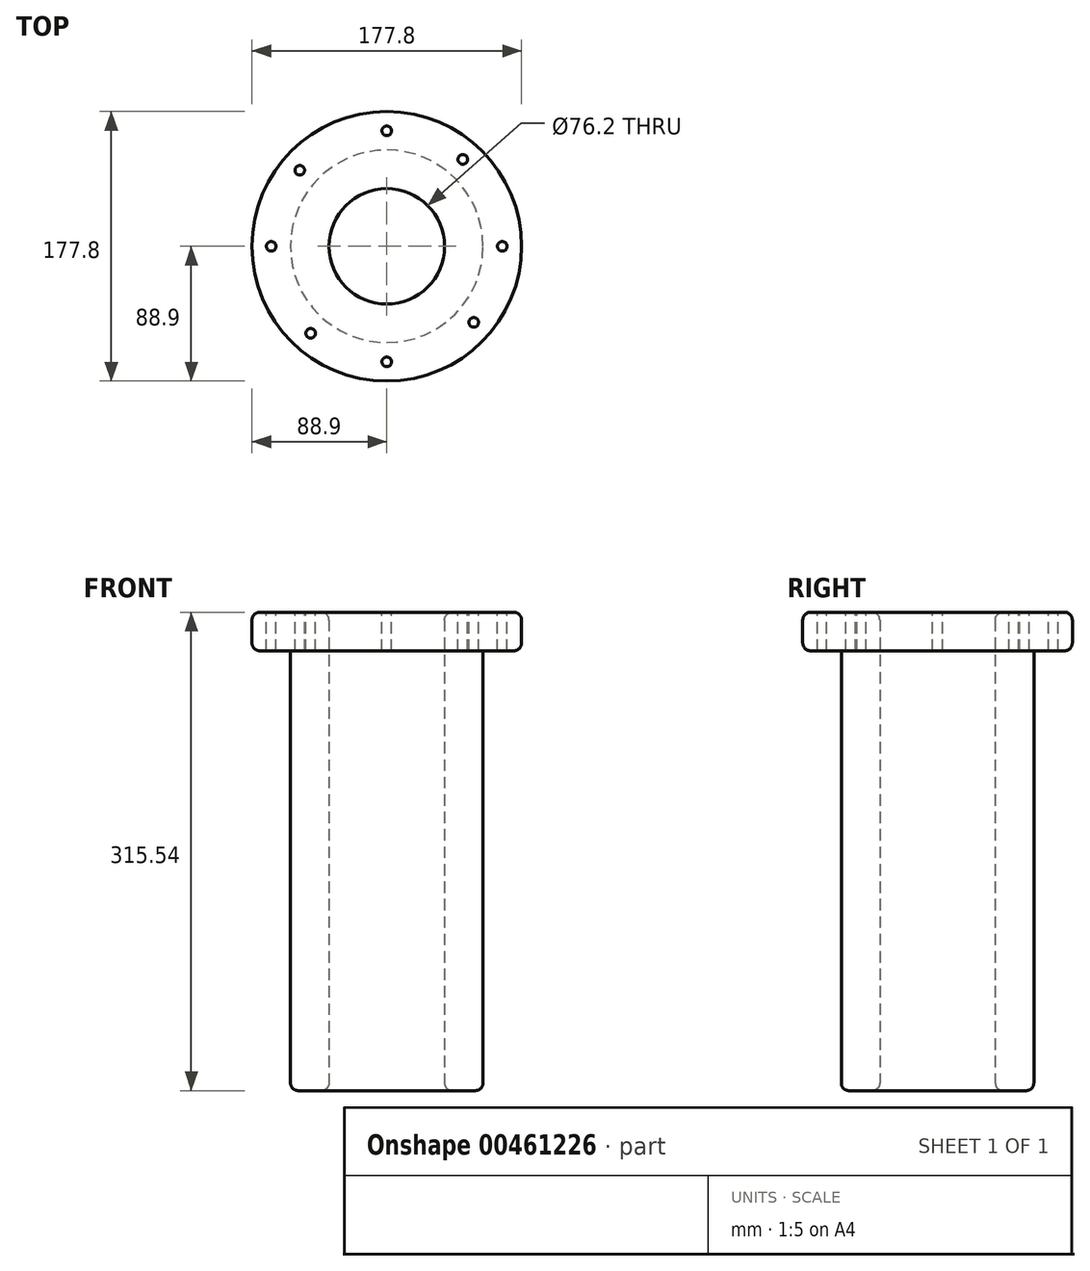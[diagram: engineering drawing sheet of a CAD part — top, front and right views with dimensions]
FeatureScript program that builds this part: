
annotation { "Feature Type Name" : "Feature", "Feature Type Description" : "" }
export const myFeature = defineFeature(function(context is Context, id is Id, definition is map)
    precondition{}
    {
        {
            var Q0;
            Q0=qCreatedBy(makeId("Front.planeOp"),FACE);
            var sketch = newSketch(context, id + "F0", { "sketchPlane" : qUnion([Q0])});
            skLineSegment(sketch, "E0.bottom", {"start": v(63.5, -145.07) * mm, "end": v(-63.5, -145.07) * mm});
            skLineSegment(sketch, "E0.top", {"start": v(63.5, 145.07) * mm, "end": v(-63.5, 145.07) * mm});
            skLineSegment(sketch, "E0.left", {"start": v(63.5, -145.07) * mm, "end": v(63.5, 145.07) * mm});
            skLineSegment(sketch, "E0.right", {"start": v(-63.5, -145.07) * mm, "end": v(-63.5, 145.07) * mm});
            skPoint(sketch, "E0.middle", {"position": v(0, 0) * mm});
            skLineSegment(sketch, "E1", {"start": v(0, 145.07) * mm, "end": v(0, -145.07) * mm});
            skLineSegment(sketch, "E2", {"start": v(-38.1, -145.07) * mm, "end": v(-38.1, 145.07) * mm});
            skLineSegment(sketch, "E3", {"start": v(38.1, 145.07) * mm, "end": v(38.1, -145.07) * mm});
            skLineSegment(sketch, "E4", {"start": v(-88.9, 145.07) * mm, "end": v(38.1, 145.07) * mm});
            skLineSegment(sketch, "E5", {"start": v(38.1, 145.07) * mm, "end": v(38.1, 170.47) * mm});
            skLineSegment(sketch, "E6", {"start": v(38.1, 170.47) * mm, "end": v(-88.9, 170.47) * mm});
            skLineSegment(sketch, "E7", {"start": v(-88.9, 170.47) * mm, "end": v(-88.9, 145.07) * mm});
            skLineSegment(sketch, "E8", {"start": v(-38.1, 145.07) * mm, "end": v(-38.1, 170.47) * mm});
            skLineSegment(sketch, "E9", {"start": v(0, 145.07) * mm, "end": v(0, 170.47) * mm});
            skLineSegment(sketch, "E10", {"start": v(0, 170.47) * mm, "end": v(88.9, 170.47) * mm});
            skLineSegment(sketch, "E11", {"start": v(88.9, 170.47) * mm, "end": v(88.9, 145.07) * mm});
            skLineSegment(sketch, "E12", {"start": v(88.9, 145.07) * mm, "end": v(63.5, 145.07) * mm});
            skSolve(sketch);
        }
        {
            var Q0;
            {var subQ0=sQuery(id+"F0.wireOp",EDGE,"E7");Q0=makeQuery(id+"F0.imprint","IMPRINT",FACE,{"disambiguationData":[TD([[makeQuery(id+"F0.imprint","IMPRINT",EDGE,{"derivedFrom":subQ0}),1.0]])]});}
            var Q1;
            Q1=sQuery(id+"F0.wireOp",EDGE,"E9");
            revolve(context, id + "F1", {"entities" : qUnion([Q0]), "axis" : qUnion([Q1]), "revolveType" : RevolveType.FULL});
        }
        {
            var Q0;
            {var subQ0=sQuery(id+"F0.wireOp",EDGE,"E0.right");Q0=makeQuery(id+"F0.imprint","IMPRINT",FACE,{"disambiguationData":[TD([[makeQuery(id+"F0.imprint","IMPRINT",EDGE,{"derivedFrom":subQ0}),-1.0]])]});}
            var Q1;
            Q1=sQuery(id+"F0.wireOp",EDGE,"E1");
            revolve(context, id + "F2", {"operationType" : NewBodyOperationType.ADD, "entities" : qUnion([Q0]), "axis" : qUnion([Q1]), "revolveType" : RevolveType.FULL});
        }
        {
            var Q0;
            Q0=makeQuery(id+"F1.opRevolve","SWEPT_EDGE",EDGE,{"disambiguationData":[OSD([sQuery(id+"F0.wireOp",EDGE,"E6"),sQuery(id+"F0.wireOp",EDGE,"E7")])]});
            var Q1;
            Q1=makeQuery(id+"F1.opRevolve","SWEPT_EDGE",EDGE,{"disambiguationData":[OSD([sQuery(id+"F0.wireOp",EDGE,"E4"),sQuery(id+"F0.wireOp",EDGE,"E7")])]});
            var Q2;
            Q2=makeQuery(id+"F1.opRevolve","SWEPT_EDGE",EDGE,{"disambiguationData":[OSD([sQuery(id+"F0.wireOp",EDGE,"E6"),sQuery(id+"F0.wireOp",EDGE,"E8")])]});
            var Q3;
            Q3=makeQuery(id+"F2.opRevolve","SWEPT_EDGE",EDGE,{"disambiguationData":[OSD([sQuery(id+"F0.wireOp",EDGE,"E0.bottom"),sQuery(id+"F0.wireOp",EDGE,"E0.right")])]});
            fillet(context, id + "F3", {"entities" : qUnion([Q0, Q1, Q2, Q3]), "radius" : 5.08 * mm, "tangentPropagation" : true, "allowEdgeOverflow" : false});
        }
        {
            var Q0;
            Q0=makeQuery(id+"F2.opRevolve","SWEPT_EDGE",EDGE,{"disambiguationData":[OSD([sQuery(id+"F0.wireOp",EDGE,"E0.bottom"),sQuery(id+"F0.wireOp",EDGE,"E2")])]});
            fillet(context, id + "F4", {"entities" : qUnion([Q0]), "radius" : 5.08 * mm, "tangentPropagation" : true, "allowEdgeOverflow" : false});
        }
        {
            var Q0;
            Q0=makeQuery(id+"F1.opRevolve","SWEPT_FACE",FACE,{"disambiguationData":[OSD([sQuery(id+"F0.wireOp",EDGE,"E6")])]});
            var sketch = newSketch(context, id + "F5", { "sketchPlane" : qUnion([Q0])});
            skLineSegment(sketch, "E13", {"start": v(0, -65.27) * mm, "end": v(0, 65.55) * mm});
            skLineSegment(sketch, "E14", {"start": v(-63.5, 0) * mm, "end": v(64.05, 0) * mm});
            skSolve(sketch);
        }
        {
            var Q0;
            {var subQ1=sQuery(id+"F0.wireOp",EDGE,"E6");var subQ2=makeQuery(id+"F1.opRevolve","SWEPT_FACE",FACE,{"disambiguationData":[OSD([subQ1])]});Q0=makeQuery(id+"F5.imprint","IMPRINT",FACE,{"disambiguationData":[TD([[makeQuery(id+"F5.imprint","IMPRINT",EDGE,{"derivedFrom":makeQuery(id+"F3.opFillet","BLEND_EDGE",EDGE,{"blendedFrom":[makeQuery(id+"F1.opRevolve","SWEPT_EDGE",EDGE,{"disambiguationData":[OSD([subQ1,sQuery(id+"F0.wireOp",EDGE,"E7")])]}),subQ2],"blendedInto":[subQ2]})}),1.0]])]});}
            var sketch = newSketch(context, id + "F6", { "sketchPlane" : qUnion([Q0])});
            skLineSegment(sketch, "E15", {"start": v(0, 0) * mm, "end": v(0, 76.2) * mm});
            skLineSegment(sketch, "E16", {"start": v(0, 0) * mm, "end": v(76.2, 0) * mm});
            skLineSegment(sketch, "E17", {"start": v(0, 0) * mm, "end": v(-76.2, 0) * mm});
            skLineSegment(sketch, "E18", {"start": v(0, 0) * mm, "end": v(0, -76.2) * mm});
            skSolve(sketch);
        }
        {
            var Q0;
            Q0=sQuery(id+"F6.wireOp",VERTEX,"E17.end");
            var Q1;
            Q1=sQuery(id+"F6.wireOp",VERTEX,"E15.end");
            var Q2;
            Q2=makeQuery(id+"F1.opRevolve","SWEPT_BODY",BODY,{"disambiguationData":[OSD([sQuery(id+"F0.wireOp",EDGE,"E4"),sQuery(id+"F0.wireOp",EDGE,"E6"),sQuery(id+"F0.wireOp",EDGE,"E7"),sQuery(id+"F0.wireOp",EDGE,"E8")])]});
            hole(context, id + "F7", {"style" : HoleStyle.SIMPLE, "endStyle" : HoleEndStyle.THROUGH, "holeDiameter" : 6.35 * mm, "isTappedThrough" : true, "tappedDepth" : 12.7 * mm, "tapClearance" : 3, "locations" : qUnion([Q0, Q1]), "scope" : qUnion([Q2])});
        }
        {
            var Q0;
            {var subQ1=sQuery(id+"F0.wireOp",EDGE,"E6");var subQ2=makeQuery(id+"F1.opRevolve","SWEPT_FACE",FACE,{"disambiguationData":[OSD([subQ1])]});Q0=makeQuery(id+"F5.imprint","IMPRINT",FACE,{"disambiguationData":[TD([[makeQuery(id+"F5.imprint","IMPRINT",EDGE,{"derivedFrom":makeQuery(id+"F3.opFillet","BLEND_EDGE",EDGE,{"blendedFrom":[makeQuery(id+"F1.opRevolve","SWEPT_EDGE",EDGE,{"disambiguationData":[OSD([subQ1,sQuery(id+"F0.wireOp",EDGE,"E7")])]}),subQ2],"blendedInto":[subQ2]})}),1.0]])]});}
            var sketch = newSketch(context, id + "F8", { "sketchPlane" : qUnion([Q0])});
            skLineSegment(sketch, "E19", {"start": v(0, 0) * mm, "end": v(0, -76.2) * mm});
            skLineSegment(sketch, "E20", {"start": v(0, 0) * mm, "end": v(76.2, 0) * mm});
            skSolve(sketch);
        }
        {
            var Q0;
            Q0=sQuery(id+"F8.wireOp",VERTEX,"E19.end");
            var Q1;
            Q1=sQuery(id+"F8.wireOp",VERTEX,"E20.end");
            var Q2;
            Q2=makeQuery(id+"F1.opRevolve","SWEPT_BODY",BODY,{"disambiguationData":[OSD([sQuery(id+"F0.wireOp",EDGE,"E4"),sQuery(id+"F0.wireOp",EDGE,"E6"),sQuery(id+"F0.wireOp",EDGE,"E7"),sQuery(id+"F0.wireOp",EDGE,"E8")])]});
            hole(context, id + "F9", {"style" : HoleStyle.SIMPLE, "endStyle" : HoleEndStyle.THROUGH, "holeDiameter" : 6.35 * mm, "isTappedThrough" : true, "tappedDepth" : 12.7 * mm, "tapClearance" : 3, "locations" : qUnion([Q0, Q1]), "scope" : qUnion([Q2])});
        }
        {
            var Q0;
            {var subQ1=sQuery(id+"F0.wireOp",EDGE,"E6");var subQ2=makeQuery(id+"F1.opRevolve","SWEPT_FACE",FACE,{"disambiguationData":[OSD([subQ1])]});Q0=makeQuery(id+"F5.imprint","IMPRINT",FACE,{"disambiguationData":[TD([[makeQuery(id+"F5.imprint","IMPRINT",EDGE,{"derivedFrom":makeQuery(id+"F3.opFillet","BLEND_EDGE",EDGE,{"blendedFrom":[makeQuery(id+"F1.opRevolve","SWEPT_EDGE",EDGE,{"disambiguationData":[OSD([subQ1,sQuery(id+"F0.wireOp",EDGE,"E7")])]}),subQ2],"blendedInto":[subQ2]})}),1.0]])]});}
            var sketch = newSketch(context, id + "F10", { "sketchPlane" : qUnion([Q0])});
            skLineSegment(sketch, "E21", {"start": v(0, 0) * mm, "end": v(-57.36, 50.16) * mm});
            skLineSegment(sketch, "E22", {"start": v(0, 0) * mm, "end": v(50.16, 57.36) * mm});
            skLineSegment(sketch, "E23", {"start": v(0, 0) * mm, "end": v(-50.16, -57.36) * mm});
            skLineSegment(sketch, "E24", {"start": v(0, 0) * mm, "end": v(57.36, -50.16) * mm});
            skSolve(sketch);
        }
        {
            var Q0;
            Q0=sQuery(id+"F10.wireOp",VERTEX,"E21.end");
            var Q1;
            Q1=sQuery(id+"F10.wireOp",VERTEX,"E22.end");
            var Q2;
            Q2=sQuery(id+"F10.wireOp",VERTEX,"E24.end");
            var Q3;
            Q3=sQuery(id+"F10.wireOp",VERTEX,"E23.end");
            var Q4;
            Q4=makeQuery(id+"F1.opRevolve","SWEPT_BODY",BODY,{"disambiguationData":[OSD([sQuery(id+"F0.wireOp",EDGE,"E4"),sQuery(id+"F0.wireOp",EDGE,"E6"),sQuery(id+"F0.wireOp",EDGE,"E7"),sQuery(id+"F0.wireOp",EDGE,"E8")])]});
            hole(context, id + "F11", {"style" : HoleStyle.SIMPLE, "endStyle" : HoleEndStyle.THROUGH, "holeDiameter" : 6.35 * mm, "isTappedThrough" : true, "tappedDepth" : 12.7 * mm, "tapClearance" : 3, "locations" : qUnion([Q0, Q1, Q2, Q3]), "scope" : qUnion([Q4])});
        }
    });
